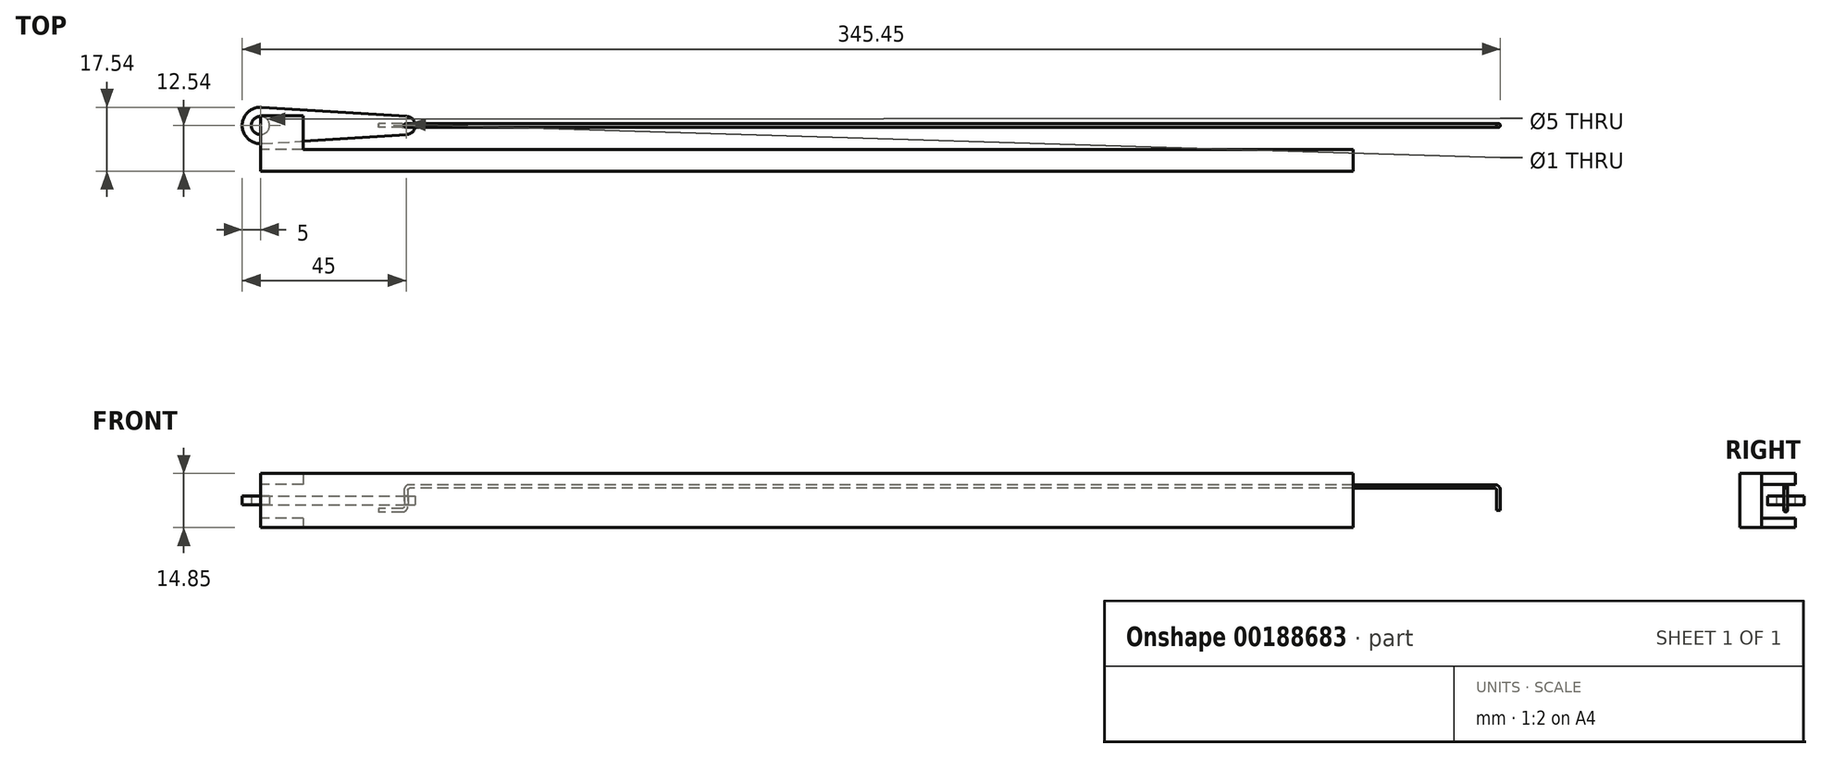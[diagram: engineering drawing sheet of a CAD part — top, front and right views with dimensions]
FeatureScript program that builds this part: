
annotation { "Feature Type Name" : "Feature", "Feature Type Description" : "" }
export const myFeature = defineFeature(function(context is Context, id is Id, definition is map)
    precondition{}
    {
        {
            var Q0;
            Q0=qCreatedBy(makeId("Top.planeOp"),FACE);
            var sketch = newSketch(context, id + "F0", { "sketchPlane" : qUnion([Q0])});
            skArc(sketch, "E0", {"start": v(0.31, 5) * mm, "mid": v(-5, 0) * mm, "end": v(0.31, -5) * mm});
            skLineSegment(sketch, "E1", {"start": v(0, 0) * mm, "end": v(40, 0) * mm, "construction": true});
            skCircle(sketch, "E2", {"center": v(40, 0) * mm, "radius": 0.5 * mm});
            skArc(sketch, "E3", {"start": v(40.16, -2.5) * mm, "mid": v(42.5, 0) * mm, "end": v(40.16, 2.5) * mm});
            skLineSegment(sketch, "E4", {"start": v(0.31, 5) * mm, "end": v(40.16, 2.5) * mm});
            skLineSegment(sketch, "E5", {"start": v(0.31, -5) * mm, "end": v(40.16, -2.5) * mm});
            skSolve(sketch);
        }
        {
            var Q0;
            Q0=makeQuery(id+"F0.imprint","IMPRINT",FACE,{"disambiguationData":[TD([[makeQuery(id+"F0.imprint","IMPRINT",EDGE,{"derivedFrom":sQuery(id+"F0.wireOp",EDGE,"E0")}),1.0]])]});
            var sketch = newSketch(context, id + "F1", { "sketchPlane" : qUnion([Q0])});
            skCircle(sketch, "E6", {"center": v(0, 0) * mm, "radius": 2.5 * mm});
            skSolve(sketch);
        }
        {
            var Q0;
            Q0=makeQuery(id+"F1.imprint","IMPRINT",FACE,{"disambiguationData":[TD([[makeQuery(id+"F1.imprint","IMPRINT",EDGE,{"derivedFrom":sQuery(id+"F1.wireOp",EDGE,"E6")}),-1.0]])]});
            extrude(context, id + "F2", {"entities" : qUnion([Q0]), "depth" : 2.5 * mm, "symmetric" : true});
        }
        {
            var Q0;
            Q0=qCreatedBy(makeId("Front.planeOp"),FACE);
            var sketch = newSketch(context, id + "F3", { "sketchPlane" : qUnion([Q0])});
            skLineSegment(sketch, "E7", {"start": v(39.95, 0) * mm, "end": v(39.95, -1.67) * mm});
            skLineSegment(sketch, "E8", {"start": v(38.95, -2.67) * mm, "end": v(32.48, -2.67) * mm});
            skLineSegment(sketch, "E9", {"start": v(39.95, 0) * mm, "end": v(39.95, 2.82) * mm});
            skLineSegment(sketch, "E10", {"start": v(40.95, 3.82) * mm, "end": v(338.95, 3.82) * mm});
            skLineSegment(sketch, "E11", {"start": v(339.95, 2.82) * mm, "end": v(339.95, -2.67) * mm});
            skPoint(sketch, "E12.visualSharp", {"position": v(339.95, 3.82) * mm});
            skArc(sketch, "E12.filletArc", {"start": v(339.95, 2.82) * mm, "mid": v(339.65, 3.53) * mm, "end": v(338.95, 3.82) * mm});
            skPoint(sketch, "E13.visualSharp", {"position": v(39.95, 3.82) * mm});
            skArc(sketch, "E13.filletArc", {"start": v(40.95, 3.82) * mm, "mid": v(40.24, 3.53) * mm, "end": v(39.95, 2.82) * mm});
            skPoint(sketch, "E14.visualSharp", {"position": v(39.95, -2.67) * mm});
            skArc(sketch, "E14.filletArc", {"start": v(38.95, -2.67) * mm, "mid": v(39.65, -2.38) * mm, "end": v(39.95, -1.67) * mm});
            skSolve(sketch);
        }
        {
            var Q0;
            Q0=sQuery(id+"F3.wireOp",VERTEX,"E11.end");
            var Q1;
            Q1=qCreatedBy(makeId("Top.planeOp"),FACE);
            cPlane(context, id + "F4", {"entities" : qUnion([Q0, Q1]), "cplaneType" : CPlaneType.PLANE_POINT, "offset" : 25 * mm, "width" : 150 * mm, "height" : 150 * mm});
        }
        {
            var Q0;
            Q0=qCreatedBy(id+"F4.planeOp",FACE);
            var sketch = newSketch(context, id + "F5", { "sketchPlane" : qUnion([Q0])});
            skCircle(sketch, "E15", {"center": v(339.95, 0) * mm, "radius": 0.5 * mm});
            skSolve(sketch);
        }
        {
            var Q0;
            Q0=makeQuery(id+"F5.imprint","IMPRINT",FACE,{"disambiguationData":[TD([[makeQuery(id+"F5.imprint","IMPRINT",EDGE,{"derivedFrom":sQuery(id+"F5.wireOp",EDGE,"E15")}),1.0]])]});
            var Q1;
            Q1=sQuery(id+"F3.wireOp",EDGE,"E11");
            var Q2;
            Q2=sQuery(id+"F3.wireOp",EDGE,"E12.filletArc");
            var Q3;
            Q3=sQuery(id+"F3.wireOp",EDGE,"E10");
            var Q4;
            Q4=sQuery(id+"F3.wireOp",EDGE,"E13.filletArc");
            var Q5;
            Q5=sQuery(id+"F3.wireOp",EDGE,"E9");
            var Q6;
            Q6=sQuery(id+"F3.wireOp",EDGE,"E7");
            var Q7;
            Q7=sQuery(id+"F3.wireOp",EDGE,"E14.filletArc");
            var Q8;
            Q8=sQuery(id+"F3.wireOp",EDGE,"E8");
            sweep(context, id + "F6", {"profiles" : qUnion([Q0]), "path" : qUnion([Q1, Q2, Q3, Q4, Q5, Q6, Q7, Q8])});
        }
        {
            var Q0;
            Q0=qCreatedBy(makeId("Right.planeOp"),FACE);
            var sketch = newSketch(context, id + "F7", { "sketchPlane" : qUnion([Q0])});
            skLineSegment(sketch, "E16.bottom", {"start": v(-12.54, 7.4) * mm, "end": v(-6.64, 7.4) * mm});
            skLineSegment(sketch, "E16.top", {"start": v(-12.54, -7.45) * mm, "end": v(-6.64, -7.45) * mm});
            skLineSegment(sketch, "E16.left", {"start": v(-12.54, 7.4) * mm, "end": v(-12.54, -7.45) * mm});
            skLineSegment(sketch, "E16.right", {"start": v(-6.64, 7.4) * mm, "end": v(-6.64, -7.45) * mm});
            skLineSegment(sketch, "E17.bottom", {"start": v(-6.64, 7.4) * mm, "end": v(2.68, 7.4) * mm});
            skLineSegment(sketch, "E17.top", {"start": v(-6.64, 4.43) * mm, "end": v(2.68, 4.43) * mm});
            skLineSegment(sketch, "E17.left", {"start": v(-6.64, 7.4) * mm, "end": v(-6.64, 4.43) * mm});
            skLineSegment(sketch, "E17.right", {"start": v(2.68, 7.4) * mm, "end": v(2.68, 4.43) * mm});
            skLineSegment(sketch, "E18.bottom", {"start": v(-6.64, -7.45) * mm, "end": v(2.68, -7.45) * mm});
            skLineSegment(sketch, "E18.top", {"start": v(-6.64, -4.87) * mm, "end": v(2.68, -4.87) * mm});
            skLineSegment(sketch, "E18.left", {"start": v(-6.64, -7.45) * mm, "end": v(-6.64, -4.87) * mm});
            skLineSegment(sketch, "E18.right", {"start": v(2.68, -7.45) * mm, "end": v(2.68, -4.87) * mm});
            skSolve(sketch);
        }
        {
            var Q0;
            Q0=makeQuery(id+"F7.imprint","IMPRINT",FACE,{"disambiguationData":[TD([[makeQuery(id+"F7.imprint","IMPRINT",EDGE,{"derivedFrom":sQuery(id+"F7.wireOp",EDGE,"E16.bottom")}),-1.0]])]});
            extrude(context, id + "F8", {"entities" : qUnion([Q0]), "depth" : 300 * mm});
        }
        {
            var Q0;
            Q0=makeQuery(id+"F7.imprint","IMPRINT",FACE,{"disambiguationData":[TD([[makeQuery(id+"F7.imprint","IMPRINT",EDGE,{"derivedFrom":sQuery(id+"F7.wireOp",EDGE,"E17.bottom")}),-1.0]])]});
            var Q1;
            Q1=makeQuery(id+"F7.imprint","IMPRINT",FACE,{"disambiguationData":[TD([[makeQuery(id+"F7.imprint","IMPRINT",EDGE,{"derivedFrom":sQuery(id+"F7.wireOp",EDGE,"E18.bottom")}),1.0]])]});
            extrude(context, id + "F9", {"entities" : qUnion([Q0, Q1]), "operationType" : NewBodyOperationType.ADD, "depth" : 11.7 * mm});
        }
    });
